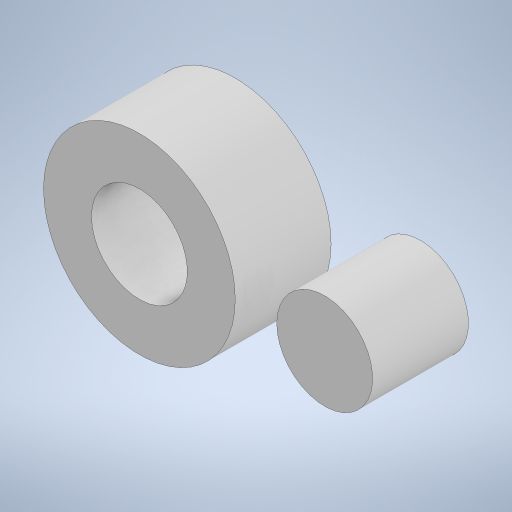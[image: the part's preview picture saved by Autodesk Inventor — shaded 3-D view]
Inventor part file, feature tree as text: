
AUTODESK INVENTOR PART (.ipt)
format: ipt  version: 2024 (Build 280153000, 153)  size: 218,624 bytes
history: native  units: mm
features: extrude x1, sketch x1
ambient origin geometry x8: Origin, YZ Plane, XZ Plane, XY Plane, X Axis, Y Axis, Z Axis, Center Point
bodies: Solid1 (feature_tree)
feature tree (2):
  extrude  "Extrusion1"  Depth=5.0mm
  sketch  "Sketch1"  dims[d0=5.0mm d1=5.0mm d2=10.0mm d3=9.665293mm d4=5.0mm d5=0.0mm]
